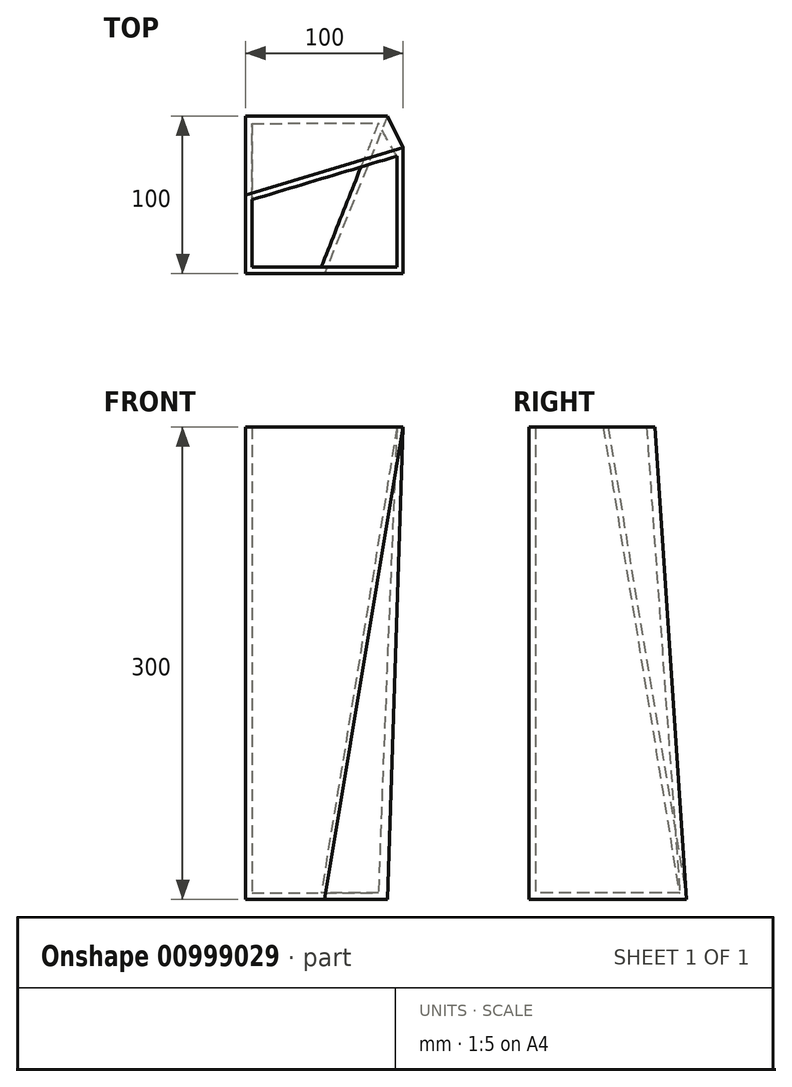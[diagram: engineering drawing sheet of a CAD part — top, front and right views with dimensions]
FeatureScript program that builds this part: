
annotation { "Feature Type Name" : "Feature", "Feature Type Description" : "" }
export const myFeature = defineFeature(function(context is Context, id is Id, definition is map)
    precondition{}
    {
        {
            var Q0;
            Q0=qCreatedBy(makeId("Top.planeOp"),FACE);
            var sketch = newSketch(context, id + "F0", { "sketchPlane" : qUnion([Q0])});
            skLineSegment(sketch, "E0", {"start": v(0, 0) * mm, "end": v(0, 100) * mm});
            skLineSegment(sketch, "E1", {"start": v(0, 100) * mm, "end": v(90, 100) * mm});
            skLineSegment(sketch, "E2", {"start": v(90, 100) * mm, "end": v(50, 0) * mm});
            skLineSegment(sketch, "E3", {"start": v(50, 0) * mm, "end": v(0, 0) * mm});
            skSolve(sketch);
        }
        {
            var Q0;
            Q0=qCreatedBy(makeId("Top.planeOp"),FACE);
            cPlane(context, id + "F1", {"entities" : qUnion([Q0]), "cplaneType" : CPlaneType.OFFSET, "offset" : 300 * mm, "width" : 150 * mm, "height" : 150 * mm});
        }
        {
            var Q0;
            Q0=qCreatedBy(id+"F1.planeOp",FACE);
            var sketch = newSketch(context, id + "F2", { "sketchPlane" : qUnion([Q0])});
            skLineSegment(sketch, "E4", {"start": v(0, 0) * mm, "end": v(100, 0) * mm});
            skLineSegment(sketch, "E5", {"start": v(100, 0) * mm, "end": v(100, 80) * mm});
            skLineSegment(sketch, "E6", {"start": v(100, 80) * mm, "end": v(0, 50) * mm});
            skLineSegment(sketch, "E7", {"start": v(0, 50) * mm, "end": v(0, 0) * mm});
            skSolve(sketch);
        }
        {
            var Q0;
            Q0=makeQuery(id+"F2.imprint","IMPRINT",FACE,{"disambiguationData":[TD([[makeQuery(id+"F2.imprint","IMPRINT",EDGE,{"derivedFrom":sQuery(id+"F2.wireOp",EDGE,"E4")}),1.0]])]});
            var Q1;
            Q1=makeQuery(id+"F0.imprint","IMPRINT",FACE,{"disambiguationData":[TD([[makeQuery(id+"F0.imprint","IMPRINT",EDGE,{"derivedFrom":sQuery(id+"F0.wireOp",EDGE,"E0")}),-1.0]])]});
            loft(context, id + "F3", {"sheetProfilesArray" : [{ "sheetProfileEntities" : qUnion([Q0]) }, { "sheetProfileEntities" : qUnion([Q1]) }]});
        }
        {
            var Q0;
            Q0=makeQuery(id+"F3.opLoft","CAP_FACE",FACE,{"disambiguationData":[OSD([makeQuery(id+"F2.imprint","IMPRINT",FACE,{"disambiguationData":[TD([[makeQuery(id+"F2.imprint","IMPRINT",EDGE,{"derivedFrom":sQuery(id+"F2.wireOp",EDGE,"E4")}),1.0]])]})])],"isStart":true});
            shell(context, id + "F4", {"entities" : qUnion([Q0]), "thickness" : 4 * mm});
        }
    });
